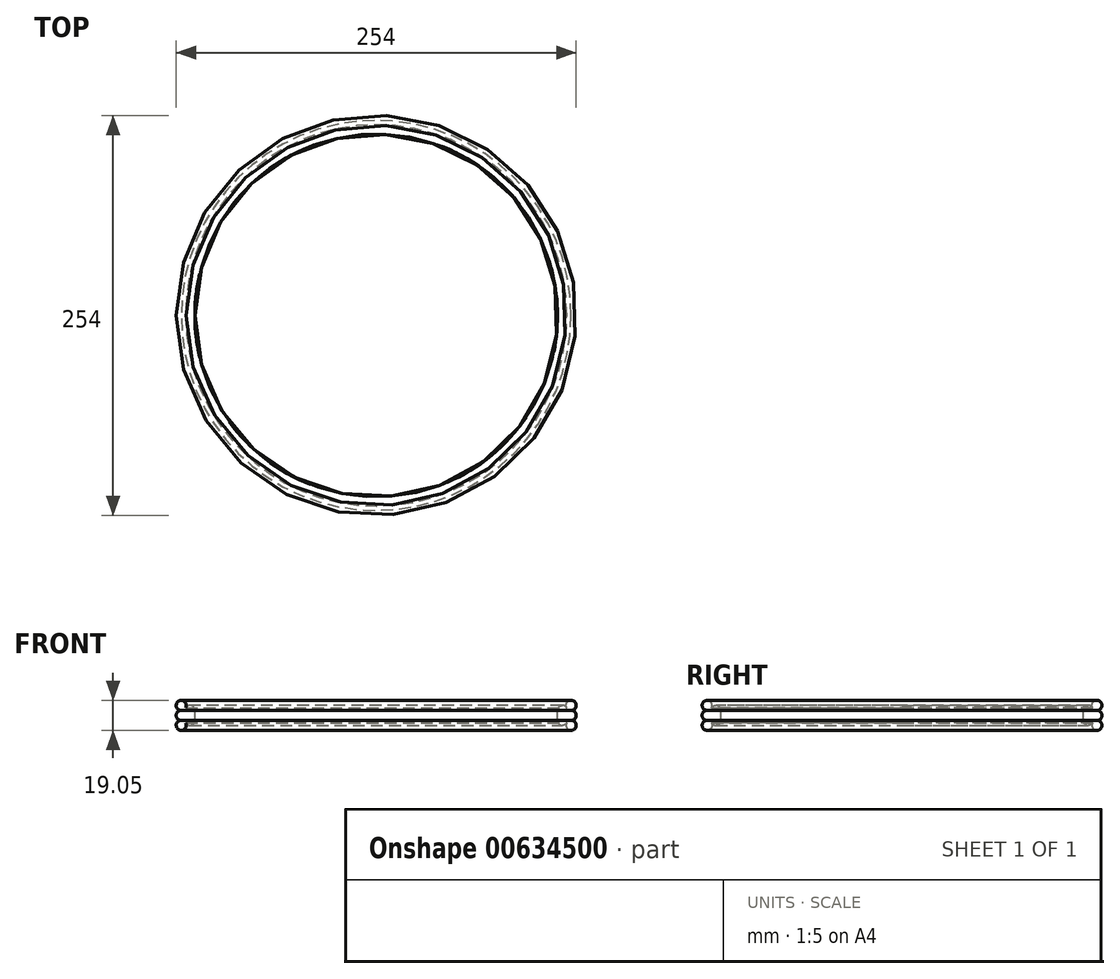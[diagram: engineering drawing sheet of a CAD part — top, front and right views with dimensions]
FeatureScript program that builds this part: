
annotation { "Feature Type Name" : "Feature", "Feature Type Description" : "" }
export const myFeature = defineFeature(function(context is Context, id is Id, definition is map)
    precondition{}
    {
        {
            var Q0;
            Q0=qCreatedBy(makeId("Front.planeOp"),FACE);
            var sketch = newSketch(context, id + "F0", { "sketchPlane" : qUnion([Q0])});
            skArc(sketch, "E0", {"start": v(3.18, 6.35) * mm, "mid": v(1.59, 0.43) * mm, "end": v(5.92, 4.76) * mm});
            skArc(sketch, "E1", {"start": v(3.18, 12.7) * mm, "mid": v(0, 9.53) * mm, "end": v(3.18, 6.35) * mm});
            skArc(sketch, "E2", {"start": v(5.92, 14.29) * mm, "mid": v(1.59, 18.62) * mm, "end": v(3.17, 12.7) * mm});
            skLineSegment(sketch, "E3", {"start": v(0, 39.44) * mm, "end": v(0, 0) * mm, "construction": true});
            skLineSegment(sketch, "E4", {"start": v(0, 0) * mm, "end": v(127, 0) * mm, "construction": true});
            skLineSegment(sketch, "E5", {"start": v(127, 0) * mm, "end": v(127, 36.5) * mm, "construction": true});
            skArc(sketch, "E6", {"start": v(5.92, 4.76) * mm, "mid": v(9.5, 3.28) * mm, "end": v(11.85, 6.35) * mm});
            skArc(sketch, "E7", {"start": v(11.85, 12.68) * mm, "mid": v(9.5, 15.76) * mm, "end": v(5.92, 14.29) * mm});
            skLineSegment(sketch, "E8", {"start": v(11.85, 12.68) * mm, "end": v(11.85, 6.35) * mm});
            skSolve(sketch);
        }
        {
            var Q0;
            Q0=makeQuery(id+"F0.imprint","IMPRINT",FACE,{"disambiguationData":[TD([[makeQuery(id+"F0.imprint","IMPRINT",EDGE,{"derivedFrom":sQuery(id+"F0.wireOp",EDGE,"E2")}),1.0]])]});
            var Q1;
            {var subQ0=sQuery(id+"F0.wireOp",EDGE,"E1");var subQ1=makeQuery(id+"F0.imprint","INTERSECT",VERTEX,{"derivedFrom":[sQuery(id+"F0.wireOp",EDGE,"E0"),subQ0]});Q1=makeQuery(id+"F0.imprint","IMPRINT",FACE,{"disambiguationData":[TD([[makeQuery(id+"F0.imprint","IMPRINT",EDGE,{"disambiguationData":[TD([[subQ1,1.0]])],"derivedFrom":subQ0}),1.0]])]});}
            var Q2;
            Q2=makeQuery(id+"F0.imprint","IMPRINT",FACE,{"disambiguationData":[TD([[makeQuery(id+"F0.imprint","IMPRINT",EDGE,{"derivedFrom":sQuery(id+"F0.wireOp",EDGE,"E0")}),1.0]])]});
            var Q3;
            Q3=sQuery(id+"F0.wireOp",EDGE,"E5");
            revolve(context, id + "F1", {"entities" : qUnion([Q0, Q1, Q2]), "axis" : qUnion([Q3]), "revolveType" : RevolveType.FULL});
        }
    });
